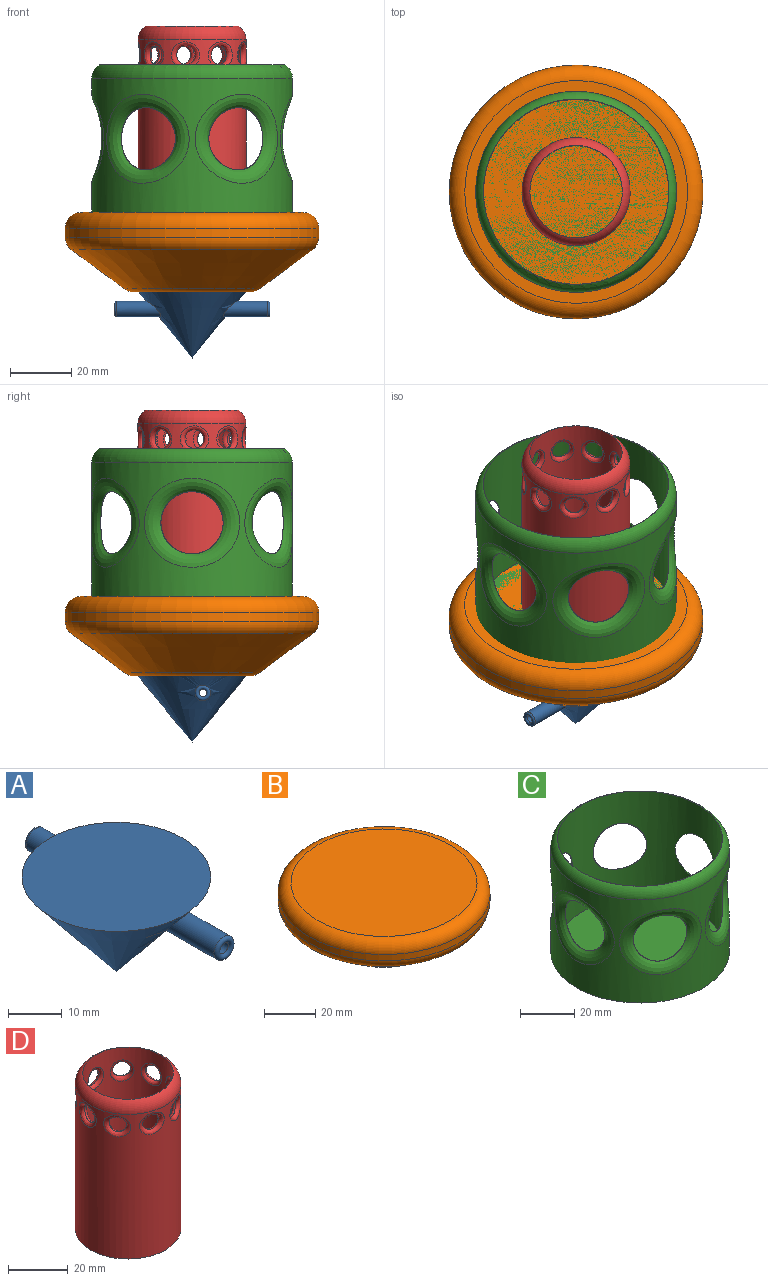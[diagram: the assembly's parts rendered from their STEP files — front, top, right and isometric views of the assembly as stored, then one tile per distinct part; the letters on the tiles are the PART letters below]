
ASSEMBLY  parts=4 mates=3
PART A: 12 faces, bbox 35.3x50.8x21.6 mm
  f0: plane 35.28x35.28mm, normal (0,0,1), area 977.8mm2, adj f1
  f1: cone r=17.64mm half-angle=39.2deg, axis (0,0,1), area 1493mm2, adj f0,f2,f3
  f2: cylinder r=2.51mm len=14.51mm, axis (0,-1,0), area 194.3mm2, adj f1,f11
  f3: cylinder r=2.51mm len=14.51mm, axis (0,-1,0), area 194.2mm2, adj f1,f10
  f4: plane 29.93x29.93mm, normal (0,0,-1), area 703.7mm2, adj f5
  f5: cone r=16.66mm half-angle=39.2deg, axis (0,0,1), area 1084.2mm2, adj f4,f8,f9
  f6: cylinder r=1.24mm len=14.77mm, axis (0,-1,0), area 102.4mm2, adj f9,f11
  f7: cylinder r=1.24mm len=14.77mm, axis (0,-1,0), area 102.4mm2, adj f8,f10
  f8: bspline ~3.88x3.76mm, area 10.8mm2, adj f5,f7
  f9: bspline ~3.88x3.76mm, area 10.8mm2, adj f5,f6
  f10: torus R=1.88mm, axis (0,-1,0), area 23.6mm2, adj f3,f7
  f11: torus R=1.88mm, axis (0,-1,0), area 23.6mm2, adj f2,f6
PART B: 7 faces, bbox 89.8x89.8x25.9 mm
  f0: cone r=41.48mm half-angle=53.7deg, axis (0,0,1), area 4152.7mm2, adj f4,f6
  f1: plane 38.15x38.15mm, normal (0,0,-1), area 1143mm2, adj f4
  f2: plane 72.8x72.8mm, normal (0,0,1), area 4162.3mm2, adj f5
  f3: cylinder r=41.48mm len=82.96mm, axis (0,0,1), area 798.1mm2, adj f5,f6
  f4: torus R=19.07mm, axis (0,0,-1), area 417.2mm2, adj f0,f1
  f5: torus R=36.4mm, axis (0,0,-1), area 1987.1mm2, adj f2,f3
  f6: torus R=36.4mm, axis (0,0,-1), area 1219.6mm2, adj f0,f3
PART C: 17 faces, bbox 71x71x51.5 mm
  f0: cylinder r=32.82mm len=65.63mm, axis (0,0,-1), area 5142.9mm2, adj f1,f4,f5,f6,f7,f8,f9,f10
  f1: plane 65.63x65.63mm, normal (0,0,-1), area 3383.2mm2, adj f0
  f2: cylinder r=30.28mm len=60.55mm, axis (0,0,-1), area 7200.8mm2, adj f3,f7,f11,f12,f13,f14,f15,f16
  f3: plane 60.55x60.55mm, normal (0,0,1), area 2879.7mm2, adj f2
  f4: bspline ~31.08x29.07mm, area 435.7mm2, adj f0,f11
  f5: bspline ~29.1x26.94mm, area 435.7mm2, adj f0,f12
  f6: bspline ~29.1x26.94mm, area 435.7mm2, adj f0,f13
  f7: bspline ~31.08x29.07mm, area 437.1mm2, adj f0,f2
  f8: bspline ~29.1x26.94mm, area 435.7mm2, adj f0,f14
  f9: bspline ~29.1x26.94mm, area 435.7mm2, adj f0,f15
  f10: torus R=27.74mm, axis (0,0,1), area 1063.3mm2, adj f0,f16
  f11: bspline ~20.35x20.34mm, area 1.7mm2, adj f2,f4
  f12: bspline ~20.34x17.63mm, area 1.7mm2, adj f2,f5
  f13: bspline ~20.34x17.64mm, area 1.7mm2, adj f2,f6
  f14: bspline ~20.34x17.63mm, area 1.7mm2, adj f2,f8
  f15: bspline ~20.34x17.64mm, area 1.7mm2, adj f2,f9
  f16: torus R=30.29mm, axis (0,0,-1), area 5.1mm2, adj f2,f10
PART D: 23 faces, bbox 38.2x38.2x64.2 mm
  f0: cylinder r=17.65mm len=59.1mm, axis (0,0,-1), area 5972.8mm2, adj f1,f4,f6,f8,f10,f12,f14,f16
  f1: plane 35.31x35.31mm, normal (0,0,-1), area 979mm2, adj f0
  f2: cylinder r=15.11mm len=60.96mm, axis (0,0,-1), area 5290mm2, adj f3,f4,f5,f7,f9,f11,f13,f15
  f3: plane 30.23x30.23mm, normal (0,0,1), area 717.5mm2, adj f2
  f4: torus R=12.57mm, axis (0,0,1), area 560.7mm2, adj f0,f2
  f5: bspline ~8.7x8.03mm, area 40mm2, adj f2,f6
  f6: bspline ~9.36x8.69mm, area 49.3mm2, adj f0,f5
  f7: bspline ~8.7x6.01mm, area 40mm2, adj f2,f8
  f8: bspline ~8.69x6.88mm, area 49.3mm2, adj f0,f7
  f9: bspline ~8.7x7.98mm, area 40mm2, adj f2,f10
  f10: bspline ~9.3x8.69mm, area 49.3mm2, adj f0,f9
  f11: bspline ~8.7x6.76mm, area 40mm2, adj f2,f12
  f12: bspline ~8.69x7.88mm, area 49.3mm2, adj f0,f11
  f13: bspline ~8.7x7.68mm, area 40mm2, adj f2,f14
  f14: bspline ~8.95x8.69mm, area 49.3mm2, adj f0,f13
  f15: bspline ~8.7x7.41mm, area 40mm2, adj f2,f16
  f16: bspline ~8.69x8.64mm, area 49.3mm2, adj f0,f15
  f17: bspline ~8.7x7.15mm, area 40mm2, adj f2,f18
  f18: bspline ~8.69x8.34mm, area 49.3mm2, adj f0,f17
  f19: bspline ~8.7x7.84mm, area 40mm2, adj f2,f20
  f20: bspline ~9.14x8.69mm, area 49.3mm2, adj f0,f19
  f21: bspline ~8.7x6.44mm, area 40mm2, adj f2,f22
  f22: bspline ~8.69x7.47mm, area 49.3mm2, adj f0,f21
PLACE A rot(axis=(0,0,-1),90deg) t=(20.74,20.89,-0.01)mm
PLACE B at identity
PLACE C t=(0,0,-2.54)mm
PLACE D rot(axis=(0,0,1),90deg) t=(20.74,-20.74,-5.08)mm
MATE cylindrical D.f0 <-> C.f0  axis (0,0,1) through (20.74,0,0)mm
MATE revolute C.f0 <-> B.f0  axis (0,0,1) through (20.74,0,0)mm
MATE revolute A.f1 <-> B.f0  axis (0,0,1) through (20.74,0,-25.95)mm
